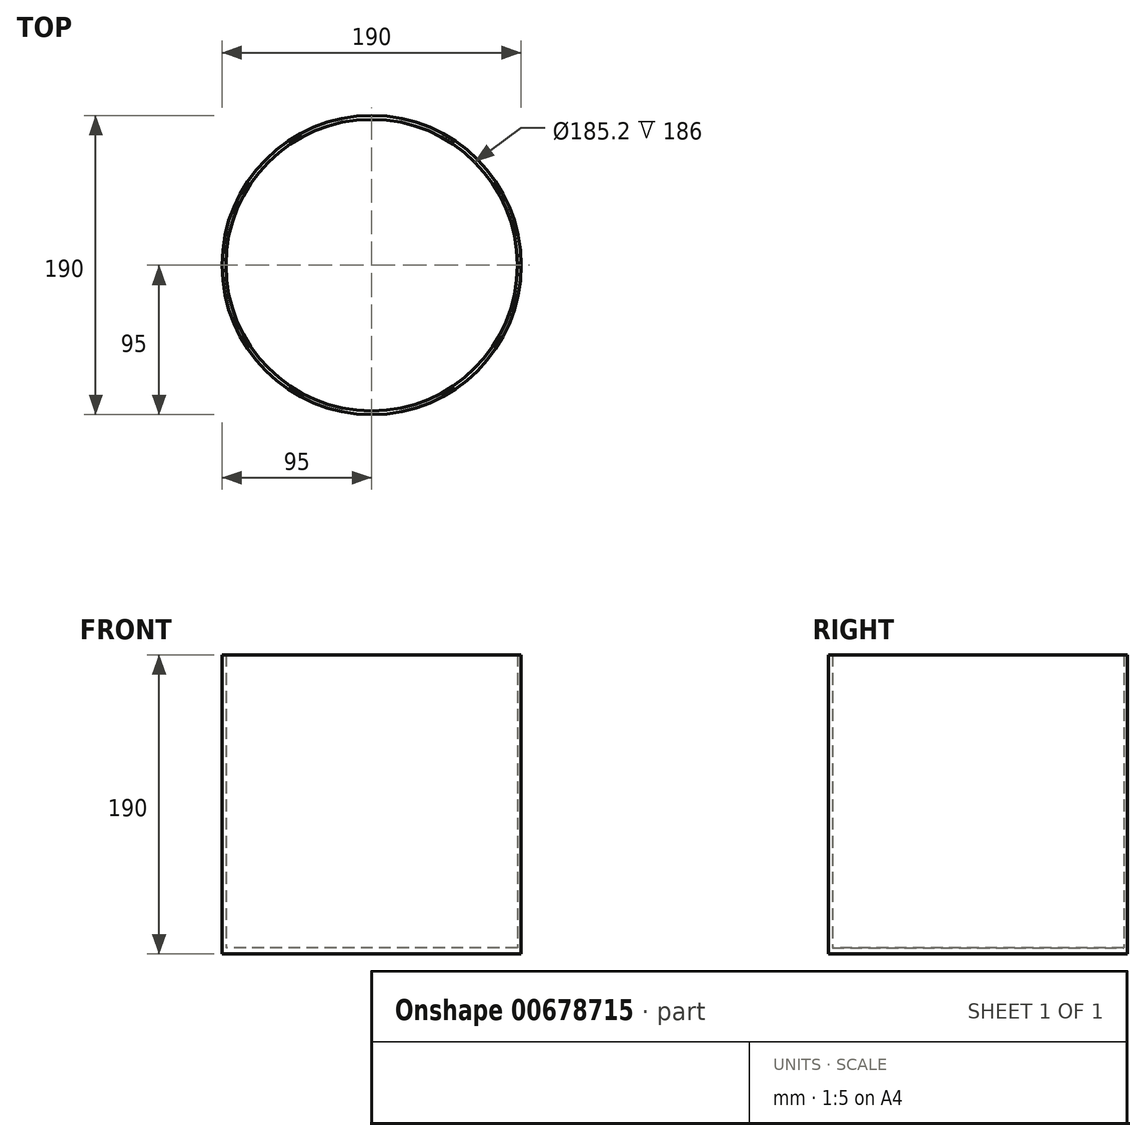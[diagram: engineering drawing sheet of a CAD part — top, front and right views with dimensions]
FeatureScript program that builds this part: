
annotation { "Feature Type Name" : "Feature", "Feature Type Description" : "" }
export const myFeature = defineFeature(function(context is Context, id is Id, definition is map)
    precondition{}
    {
        {
            var Q0;
            Q0=qCreatedBy(makeId("Top.planeOp"),FACE);
            var sketch = newSketch(context, id + "F0", { "sketchPlane" : qUnion([Q0])});
            skLineSegment(sketch, "E0.bottom", {"start": v(-85, 10) * mm, "end": v(85, 10) * mm, "construction": true});
            skLineSegment(sketch, "E0.top", {"start": v(-85, -10) * mm, "end": v(85, -10) * mm, "construction": true});
            skLineSegment(sketch, "E0.left", {"start": v(-85, 10) * mm, "end": v(-85, -10) * mm, "construction": true});
            skLineSegment(sketch, "E0.right", {"start": v(85, 10) * mm, "end": v(85, -10) * mm, "construction": true});
            skCircle(sketch, "E1", {"center": v(0, 0) * mm, "radius": 95 * mm});
            skCircle(sketch, "E2.0", {"center": v(0, 0) * mm, "radius": 92.6 * mm});
            skSolve(sketch);
        }
        {
            var Q0;
            Q0=makeQuery(id+"F0.imprint","IMPRINT",FACE,{"disambiguationData":[TD([[makeQuery(id+"F0.imprint","IMPRINT",EDGE,{"derivedFrom":sQuery(id+"F0.wireOp",EDGE,"E2.0")}),1.0]])]});
            extrude(context, id + "F1", {"entities" : qUnion([Q0]), "depth" : 4 * mm, "offsetDistance" : 25 * mm});
        }
        {
            var Q0;
            Q0=makeQuery(id+"F0.imprint","IMPRINT",FACE,{"disambiguationData":[TD([[makeQuery(id+"F0.imprint","IMPRINT",EDGE,{"derivedFrom":sQuery(id+"F0.wireOp",EDGE,"E1")}),1.0]])]});
            extrude(context, id + "F2", {"entities" : qUnion([Q0]), "operationType" : NewBodyOperationType.ADD, "depth" : 190 * mm, "offsetDistance" : 25 * mm});
        }
    });
